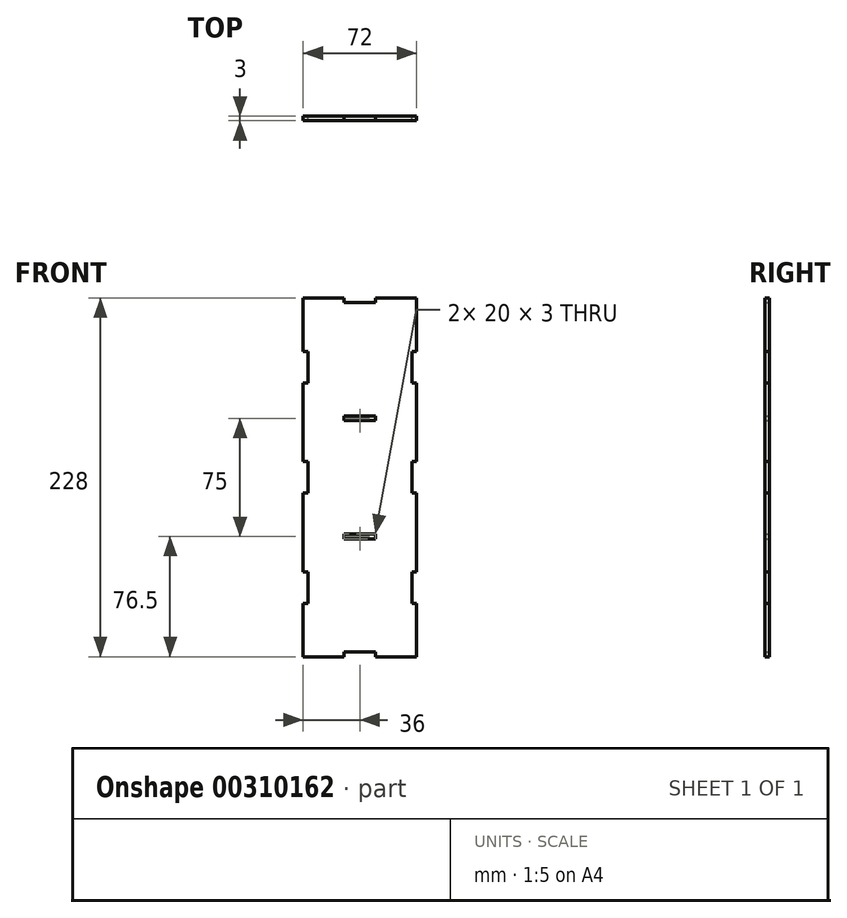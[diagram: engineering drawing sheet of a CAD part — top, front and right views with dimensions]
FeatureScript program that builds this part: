
annotation { "Feature Type Name" : "Feature", "Feature Type Description" : "" }
export const myFeature = defineFeature(function(context is Context, id is Id, definition is map)
    precondition{}
    {
        {
            var Q0;
            Q0=qCreatedBy(makeId("Front.planeOp"),FACE);
            var sketch = newSketch(context, id + "F0", { "sketchPlane" : qUnion([Q0])});
            skLineSegment(sketch, "E0.top", {"start": v(36, 114) * mm, "end": v(10, 114) * mm});
            skLineSegment(sketch, "E0.right", {"start": v(-36, -114) * mm, "end": v(-36, -80) * mm});
            skPoint(sketch, "E0.middle", {"position": v(0, 0) * mm});
            skLineSegment(sketch, "E1.top", {"start": v(10, 111) * mm, "end": v(-10, 111) * mm});
            skLineSegment(sketch, "E1.left", {"start": v(10, 114) * mm, "end": v(10, 111) * mm});
            skLineSegment(sketch, "E1.right", {"start": v(-10, 114) * mm, "end": v(-10, 111) * mm});
            skLineSegment(sketch, "E2.trimOffspring", {"start": v(-10, 114) * mm, "end": v(-36, 114) * mm});
            skLineSegment(sketch, "E3.MirrorCS", {"start": v(-10, -114) * mm, "end": v(-36, -114) * mm});
            skLineSegment(sketch, "E4.MirrorCS", {"start": v(36, -114) * mm, "end": v(10, -114) * mm});
            skLineSegment(sketch, "E5.MirrorCS", {"start": v(10, -114) * mm, "end": v(10, -111) * mm});
            skLineSegment(sketch, "E6.MirrorCS", {"start": v(10, -111) * mm, "end": v(-10, -111) * mm});
            skLineSegment(sketch, "E7.MirrorCS", {"start": v(-10, -114) * mm, "end": v(-10, -111) * mm});
            skLineSegment(sketch, "E8.bottom", {"start": v(-36, 80) * mm, "end": v(-33, 80) * mm});
            skLineSegment(sketch, "E8.top", {"start": v(-36, 60) * mm, "end": v(-33, 60) * mm});
            skLineSegment(sketch, "E8.right", {"start": v(-33, 80) * mm, "end": v(-33, 60) * mm});
            skLineSegment(sketch, "E9.bottom", {"start": v(-36, 10) * mm, "end": v(-33, 10) * mm});
            skLineSegment(sketch, "E9.top", {"start": v(-36, -10) * mm, "end": v(-33, -10) * mm});
            skLineSegment(sketch, "E9.right", {"start": v(-33, 10) * mm, "end": v(-33, -10) * mm});
            skLineSegment(sketch, "E10.bottom", {"start": v(-36, -60) * mm, "end": v(-33, -60) * mm});
            skLineSegment(sketch, "E10.top", {"start": v(-36, -80) * mm, "end": v(-33, -80) * mm});
            skLineSegment(sketch, "E10.right", {"start": v(-33, -60) * mm, "end": v(-33, -80) * mm});
            skLineSegment(sketch, "E11.trimOffspring", {"start": v(-36, 80) * mm, "end": v(-36, 114) * mm});
            skLineSegment(sketch, "E12.trimOffspring", {"start": v(-36, 10) * mm, "end": v(-36, 60) * mm});
            skLineSegment(sketch, "E13.trimOffspring", {"start": v(-36, -60) * mm, "end": v(-36, -10) * mm});
            skPoint(sketch, "E0.left.start.orphan", {"position": v(36, -114) * mm});
            skLineSegment(sketch, "E14.MirrorCS", {"start": v(36, 80) * mm, "end": v(33, 80) * mm});
            skLineSegment(sketch, "E15.MirrorCS", {"start": v(36, 60) * mm, "end": v(33, 60) * mm});
            skLineSegment(sketch, "E16.MirrorCS", {"start": v(36, -60) * mm, "end": v(33, -60) * mm});
            skLineSegment(sketch, "E17.MirrorCS", {"start": v(36, -10) * mm, "end": v(33, -10) * mm});
            skLineSegment(sketch, "E18.MirrorCS", {"start": v(36, -80) * mm, "end": v(33, -80) * mm});
            skLineSegment(sketch, "E19.MirrorCS", {"start": v(36, 10) * mm, "end": v(33, 10) * mm});
            skLineSegment(sketch, "E20.MirrorCS", {"start": v(36, 80) * mm, "end": v(36, 114) * mm});
            skLineSegment(sketch, "E21.MirrorCS", {"start": v(33, 10) * mm, "end": v(33, -10) * mm});
            skLineSegment(sketch, "E22.MirrorCS", {"start": v(36, -60) * mm, "end": v(36, -10) * mm});
            skLineSegment(sketch, "E23.MirrorCS", {"start": v(36, 10) * mm, "end": v(36, 60) * mm});
            skLineSegment(sketch, "E24.MirrorCS", {"start": v(33, -60) * mm, "end": v(33, -80) * mm});
            skLineSegment(sketch, "E25.MirrorCS", {"start": v(36, -114) * mm, "end": v(36, -80) * mm});
            skLineSegment(sketch, "E26.MirrorCS", {"start": v(33, 80) * mm, "end": v(33, 60) * mm});
            skLineSegment(sketch, "E27.bottom", {"start": v(10, 36) * mm, "end": v(-10, 36) * mm});
            skLineSegment(sketch, "E27.top", {"start": v(10, 39) * mm, "end": v(-10, 39) * mm});
            skLineSegment(sketch, "E27.left", {"start": v(10, 36) * mm, "end": v(10, 39) * mm});
            skLineSegment(sketch, "E27.right", {"start": v(-10, 36) * mm, "end": v(-10, 39) * mm});
            skPoint(sketch, "E27.middle", {"position": v(0, 37.5) * mm});
            skLineSegment(sketch, "E28.MirrorCS", {"start": v(-10, -36) * mm, "end": v(-10, -39) * mm});
            skLineSegment(sketch, "E29.MirrorCS", {"start": v(10, -36) * mm, "end": v(10, -39) * mm});
            skLineSegment(sketch, "E30.MirrorCS", {"start": v(10, -36) * mm, "end": v(-10, -36) * mm});
            skLineSegment(sketch, "E31.MirrorCS", {"start": v(10, -39) * mm, "end": v(-10, -39) * mm});
            skPoint(sketch, "E32.MirrorP", {"position": v(0, -37.5) * mm});
            skSolve(sketch);
        }
        {
            var Q0;
            Q0 = qSketchRegion(id + "F0", true);
            extrude(context, id + "F1", {"entities" : qUnion([Q0]), "depth" : 3 * mm});
        }
    });
